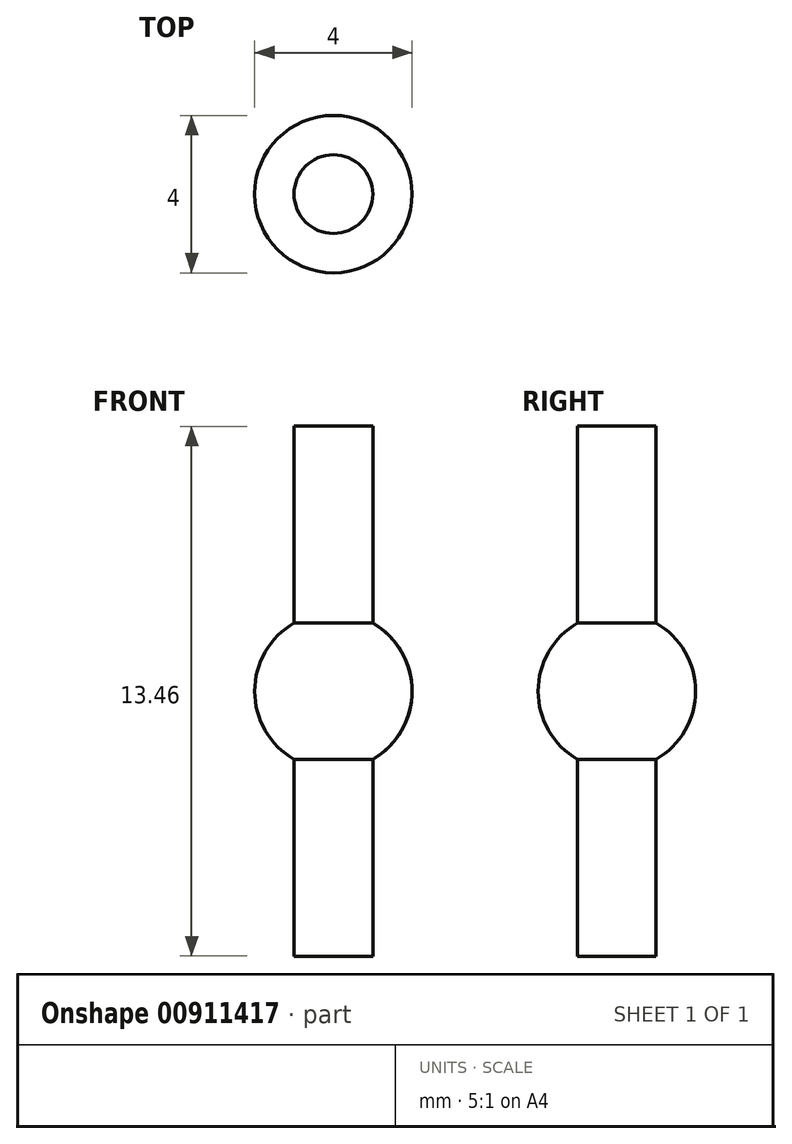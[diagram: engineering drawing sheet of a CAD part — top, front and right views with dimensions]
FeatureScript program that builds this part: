
annotation { "Feature Type Name" : "Feature", "Feature Type Description" : "" }
export const myFeature = defineFeature(function(context is Context, id is Id, definition is map)
    precondition{}
    {
        {
            var Q0;
            Q0=qCreatedBy(makeId("Front.planeOp"),FACE);
            var sketch = newSketch(context, id + "F0", { "sketchPlane" : qUnion([Q0])});
            skLineSegment(sketch, "E0", {"start": v(0, 0) * mm, "end": v(-2, 0) * mm, "construction": true});
            skLineSegment(sketch, "E1", {"start": v(0, 6.73) * mm, "end": v(0, 0) * mm, "construction": true});
            skArc(sketch, "E2", {"start": v(-2, 0) * mm, "mid": v(-1.73, 1) * mm, "end": v(-1, 1.73) * mm});
            skLineSegment(sketch, "E3", {"start": v(-1, 1.73) * mm, "end": v(-1, 6.73) * mm});
            skLineSegment(sketch, "E4", {"start": v(-1, 6.73) * mm, "end": v(0, 6.73) * mm});
            skLineSegment(sketch, "E5.MirrorCS", {"start": v(-1, -1.73) * mm, "end": v(-1, -6.73) * mm});
            skLineSegment(sketch, "E6.MirrorCS", {"start": v(-1, -6.73) * mm, "end": v(0, -6.73) * mm});
            skArc(sketch, "E7.MirrorCS", {"start": v(-2, 0) * mm, "mid": v(-1.73, -1) * mm, "end": v(-1, -1.73) * mm});
            skLineSegment(sketch, "E8", {"start": v(0, 6.73) * mm, "end": v(0, -6.73) * mm});
            skSolve(sketch);
        }
        {
            var Q0;
            Q0 = qSketchRegion(id + "F0", true);
            var Q1;
            Q1=sQuery(id+"F0.wireOp",EDGE,"E8");
            revolve(context, id + "F1", {"surfaceOperationType" : NewSurfaceOperationType.NEW, "entities" : qUnion([Q0]), "axis" : qUnion([Q1]), "revolveType" : RevolveType.FULL});
        }
    });
